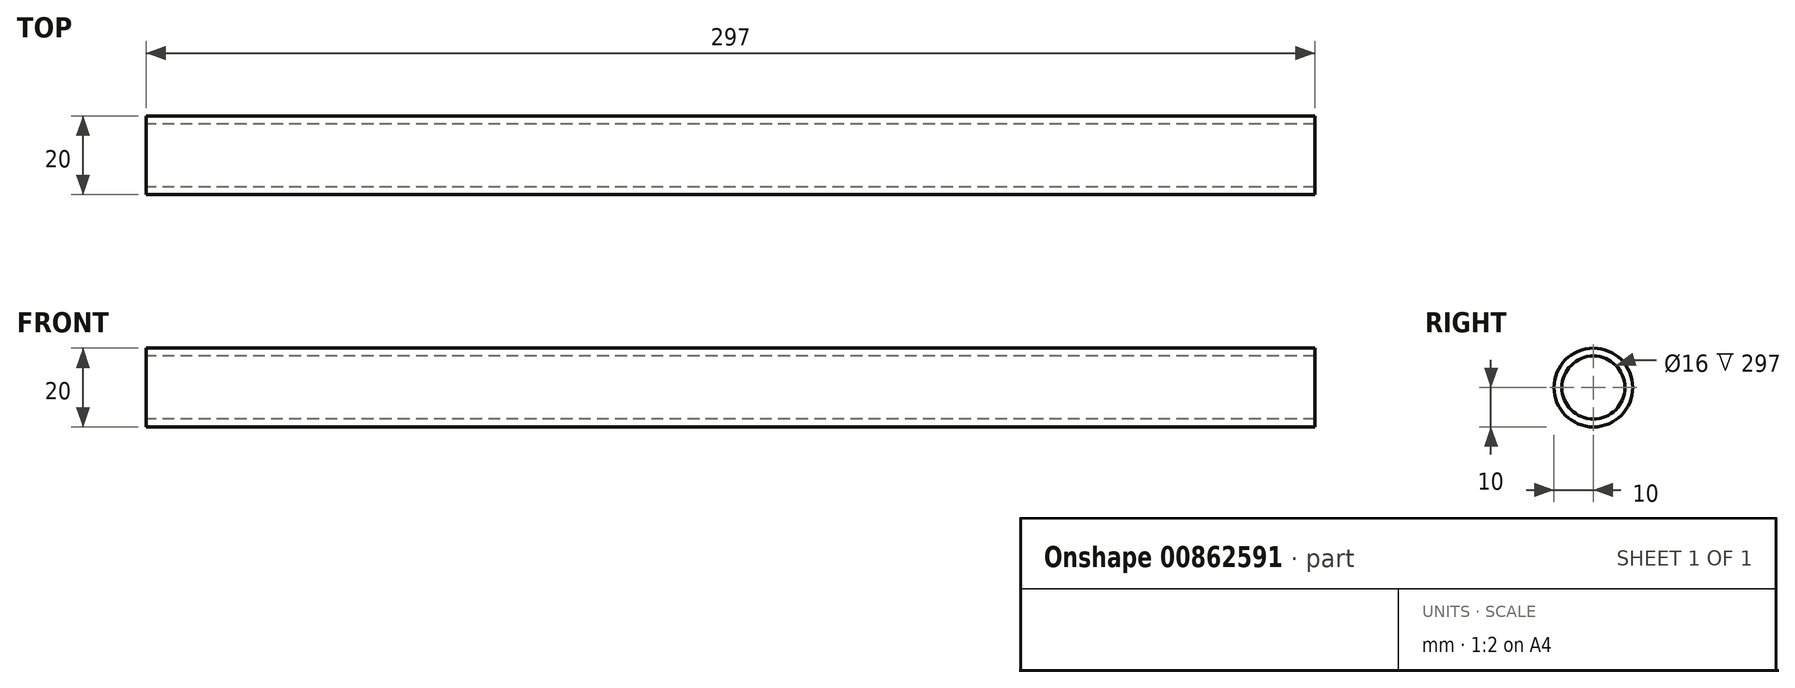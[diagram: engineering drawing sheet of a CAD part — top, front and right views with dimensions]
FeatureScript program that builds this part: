
annotation { "Feature Type Name" : "Feature", "Feature Type Description" : "" }
export const myFeature = defineFeature(function(context is Context, id is Id, definition is map)
    precondition{}
    {
        {
            var Q0;
            Q0=qCreatedBy(makeId("Front.planeOp"),FACE);
            var sketch = newSketch(context, id + "F0", { "sketchPlane" : qUnion([Q0])});
            skLineSegment(sketch, "E0", {"start": v(0, 0) * mm, "end": v(-297, 0) * mm});
            skSolve(sketch);
        }
        {
            var Q0;
            Q0=qCreatedBy(makeId("Right.planeOp"),FACE);
            var sketch = newSketch(context, id + "F1", { "sketchPlane" : qUnion([Q0])});
            skCircle(sketch, "E1", {"center": v(0, 0) * mm, "radius": 10 * mm});
            skCircle(sketch, "E2.0", {"center": v(0, 0) * mm, "radius": 8 * mm});
            skSolve(sketch);
        }
        {
            var Q0;
            Q0=makeQuery(id+"F1.imprint","IMPRINT",FACE,{"disambiguationData":[TD([[makeQuery(id+"F1.imprint","IMPRINT",EDGE,{"derivedFrom":sQuery(id+"F1.wireOp",EDGE,"E1")}),1.0]])]});
            var Q1;
            Q1=qSketchRegion(id+"F0",true);
            var Q2;
            Q2=sQuery(id+"F0.wireOp",EDGE,"E0");
            var Q3;
            Q3=sQuery(id+"F0.wireOp",EDGE,"p5A3UMdK-bUuJ-hKgG-gMdl-WLMVe5IsXQ4y");
            var Q4;
            Q4=sQuery(id+"F0.wireOp",EDGE,"jqzmJtes-IEFJ-0xae-phxS-a4aVOckqLKgL");
            sweep(context, id + "F2", {"profiles" : qUnion([Q0, Q1]), "path" : qUnion([Q2, Q3, Q4])});
        }
    });
